# Revit family: HVAC_Heaters_Enertech_CTC-EcoZenith-i555
name_source: partatom
category: Specialty Equipment
revit_build: Autodesk Revit 2017 (Build: 20190508_0315(x64)
units: mm (PartAtom-declared; Revit-internal decimal feet)

## family parameters
Always vertical = Yes
Cut with Voids When Loaded = No
OmniClass Number = 23.75.00.00
OmniClass Title = Climate Control (HVAC)
Part Type = Normal
Room Calculation Point = No
Round Connector Dimension = Use Diameter
Shared = No
Work Plane-Based = No

## types (3) — shared parameters
AssetType = Fixed
BIMObjectName = HVAC_Heaters_Enertech_CTC-EcoZenith-i555
Brand = CTC
Category = Indoor Module
Color = grey
ConvergoRefNr = 0091-1710-0016-SE
DurationUnit = Year
ElectricalDeviceNominalPower = 18000 W
EnergyClassHeatingWithControl = A++ / A+
EnergyClass_HotWater_TapProfile = A / XXL
HasProtectiveEarth = Yes
HotTapWaterPerformance = > 600 liters
IP_Code = IP X1
IfcExportAs = IfcElectricalDeviceCommon
IfcExportType = HEATER
Manufacturer = Enertech AB
ManufacturerCountry = Sweden
ManufacturerName = Enertech AB
ManufacturerURL = https://ctc.se
Material = Steel/copper
MaxOperatingPressureHotWater = 10 bar
MaxOperatingPressureThermalStore = 2.5 bar
MinimumCeilingHeight = 1950 mm
Model = CTC EcoZenith i550 Pro
NBSDescription = Air to water heat pumps
NBSReference = 90-40-40/320
Name = CTC-EcoZenith-i555
NominalCurrent = 0 A
NominalDepth = 1067 mm  [stored 3.50066 ft]
NominalFrequencyRange = 50 Hz
NominalHeight = 1700 mm  [stored 5.57743 ft]
NominalWidth = 886 mm  [stored 2.90682 ft]
PhaseAngle = 0.00°
PowerFactor = 0 W
PumpMainMaterial = Stainless Steel
PumpSecondaryMaterial = Copper
Revision = 4
Shape = Rectangular
Size = 1067x886x1700 mm
Touchscreen = yes
UNSPSCCode = 40102003
URL = https://ctc-heating.com
Uniclass2 = Pr_40_70_65
Uniclass2015Description = Preparation catering equipment
Uniclass2015Reference = Pr_40_70_65
UsageCurrent = 0 A
Version = 1
VersionDate = 10/11/2020
WarrantyDurationUnit = Year
WaterVolumeHeathingSystem = 540 liters
WaterVolumeWaterSuply = 11.4 liters
Weight = 260
zero-valued in all types: Cost

## per-type parameters (varying)
| type | EANNumber | GroupFuse | ModelNumber | NominalVoltage | OutputRangeIimmersionHeater | RatedHeatOutputModerate | RatedVoltage |
| CTC EcoZenith i555 - 400V3N | 7333077094522 | 50 A | 589600001 | 400 V | 0.3 - 18 kW /0.3 - 27 kW | 27 kW | 1200 V |
| CTC EcoZenith i555 - 230V1N | 7333077094539 | 50 A | 589600002 | 230 V | 1 - 9 kW | 9 kW | 230 V |
| CTC EcoZenith i555 - 230V3N | 7333077094546 | 63 A | 589600003 | 230 V | 2.35 - 14.1 kW / 2.35 - 21.15 kW | 9 kW | 690 V |

note: [stored X ft] marks values corroborated as IEEE doubles in the binary element streams (Revit-internal decimal feet)

## geometry (parser evidence)
native form markers: Sweep x6
no freeform markers — native parametric forms only
